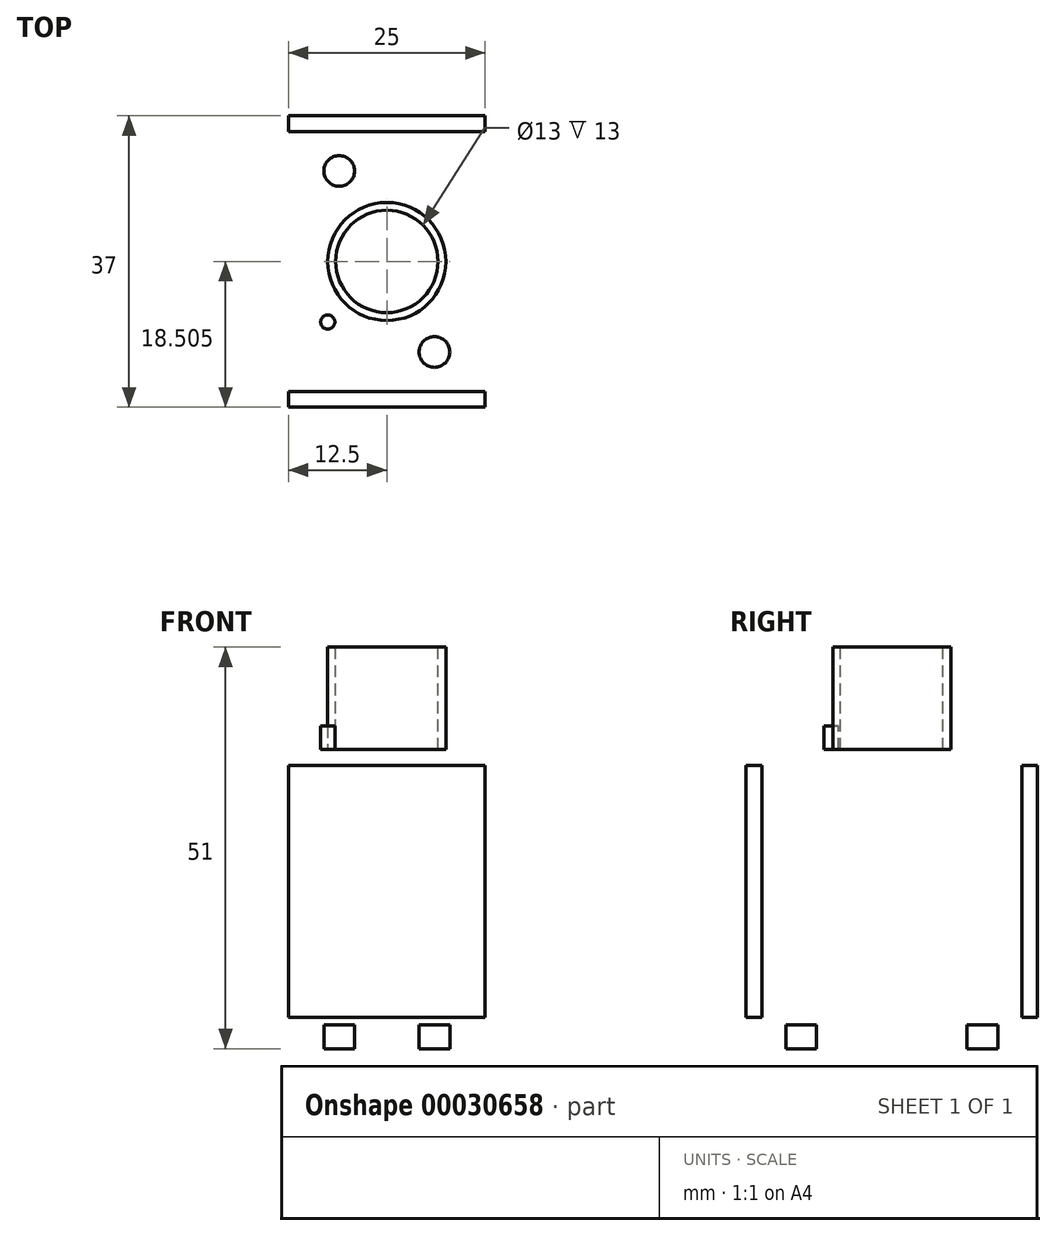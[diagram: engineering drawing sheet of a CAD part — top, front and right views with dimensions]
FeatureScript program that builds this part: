
annotation { "Feature Type Name" : "Feature", "Feature Type Description" : "" }
export const myFeature = defineFeature(function(context is Context, id is Id, definition is map)
    precondition{}
    {
        {
            var Q0;
            Q0=qCreatedBy(makeId("Right.planeOp"),FACE);
            var sketch = newSketch(context, id + "F0", { "sketchPlane" : qUnion([Q0])});
            skLineSegment(sketch, "E0.bottom", {"start": v(81.65, 0) * mm, "end": v(44.65, 0) * mm});
            skLineSegment(sketch, "E0.top", {"start": v(81.65, -41) * mm, "end": v(44.65, -41) * mm});
            skLineSegment(sketch, "E0.left", {"start": v(81.65, 0) * mm, "end": v(81.65, -41) * mm});
            skLineSegment(sketch, "E0.right", {"start": v(44.65, 0) * mm, "end": v(44.65, -41) * mm});
            skSolve(sketch);
        }
        {
            var Q0;
            Q0=makeQuery(id+"F0.imprint","IMPRINT",FACE,{"disambiguationData":[TD([[makeQuery(id+"F0.imprint","IMPRINT",EDGE,{"derivedFrom":sQuery(id+"F0.wireOp",EDGE,"E0.bottom")}),1.0]])]});
            extrude(context, id + "F1", {"entities" : qUnion([Q0]), "depth" : 25 * mm});
        }
        {
            var Q0;
            Q0=qCreatedBy(makeId("Right.planeOp"),FACE);
            var sketch = newSketch(context, id + "F2", { "sketchPlane" : qUnion([Q0])});
            skLineSegment(sketch, "E1.bottom", {"start": v(79.65, -38) * mm, "end": v(46.65, -38) * mm});
            skLineSegment(sketch, "E1.top", {"start": v(79.65, -3) * mm, "end": v(46.65, -3) * mm});
            skLineSegment(sketch, "E1.left", {"start": v(79.65, -38) * mm, "end": v(79.65, -3) * mm});
            skLineSegment(sketch, "E1.right", {"start": v(46.65, -38) * mm, "end": v(46.65, -3) * mm});
            skPoint(sketch, "E1.middle", {"position": v(63.15, -20.5) * mm});
            skPoint(sketch, "E1.middle.positionSnap0", {"position": v(81.63, -20.5) * mm});
            skPoint(sketch, "E1.centerSnap0", {"position": v(81.63, -20.5) * mm});
            skSolve(sketch);
        }
        {
            var Q0;
            Q0=makeQuery(id+"F2.imprint","IMPRINT",FACE,{"disambiguationData":[TD([[makeQuery(id+"F2.imprint","IMPRINT",EDGE,{"derivedFrom":sQuery(id+"F2.wireOp",EDGE,"u7z7irKr-tLwh-9OEY-cqf0-OPcKlIcIi4rX.bottom")}),1.0]])]});
            var Q1;
            Q1=makeQuery(id+"F2.imprint","IMPRINT",FACE,{"disambiguationData":[TD([[makeQuery(id+"F2.imprint","IMPRINT",EDGE,{"derivedFrom":sQuery(id+"F2.wireOp",EDGE,"E1.bottom")}),-1.0]])]});
            extrude(context, id + "F3", {"entities" : qUnion([Q0, Q1]), "operationType" : NewBodyOperationType.REMOVE, "depth" : 26 * mm});
        }
        {
            var Q0;
            Q0=qCreatedBy(makeId("Top.planeOp"),FACE);
            var sketch = newSketch(context, id + "F4", { "sketchPlane" : qUnion([Q0])});
            skLineSegment(sketch, "E2", {"start": v(0, 81.65) * mm, "end": v(0, 44.65) * mm});
            skLineSegment(sketch, "E3", {"start": v(0, 44.65) * mm, "end": v(25, 81.65) * mm});
            skCircle(sketch, "E4", {"center": v(12.5, 63.15) * mm, "radius": 7.5 * mm});
            skPoint(sketch, "E4.centerSnap0", {"position": v(0, 63.15) * mm});
            skCircle(sketch, "E5", {"center": v(12.5, 63.15) * mm, "radius": 6.5 * mm});
            skSolve(sketch);
        }
        {
            var Q0;
            {var subQ0=sQuery(id+"F4.wireOp",EDGE,"E5");var subQ1=sQuery(id+"F4.wireOp",EDGE,"E3");var subQ2=makeQuery(id+"F4.imprint","INTERSECT",VERTEX,{"disambiguationData":[OD(0.0)],"derivedFrom":[subQ1,subQ0]});Q0=makeQuery(id+"F4.imprint","IMPRINT",FACE,{"disambiguationData":[TD([[makeQuery(id+"F4.imprint","IMPRINT",EDGE,{"disambiguationData":[TD([[subQ2,-1.0]])],"derivedFrom":subQ1}),1.0]])]});}
            var Q1;
            {var subQ0=sQuery(id+"F4.wireOp",EDGE,"E5");var subQ1=sQuery(id+"F4.wireOp",EDGE,"E3");var subQ2=makeQuery(id+"F4.imprint","INTERSECT",VERTEX,{"disambiguationData":[OD(0.0)],"derivedFrom":[subQ1,subQ0]});Q1=makeQuery(id+"F4.imprint","IMPRINT",FACE,{"disambiguationData":[TD([[makeQuery(id+"F4.imprint","IMPRINT",EDGE,{"disambiguationData":[TD([[subQ2,-1.0]])],"derivedFrom":subQ1}),-1.0]])]});}
            extrude(context, id + "F5", {"entities" : qUnion([Q0, Q1]), "operationType" : NewBodyOperationType.REMOVE, "oppositeDirection" : true, "depth" : 25 * mm});
        }
        {
            var Q0;
            Q0 = qSketchRegion(id + "F4", true);
            extrude(context, id + "F6", {"entities" : qUnion([Q0]), "operationType" : NewBodyOperationType.ADD, "depth" : 10 * mm});
        }
        {
            var Q0;
            Q0=makeQuery(id+"F1.opExtrude","SWEPT_FACE",FACE,{"disambiguationData":[OSD([sQuery(id+"F0.wireOp",EDGE,"E0.top")])]});
            var sketch = newSketch(context, id + "F7", { "sketchPlane" : qUnion([Q0])});
            skCircle(sketch, "E6.MirrorC", {"center": v(18.55, -51.65) * mm, "radius": 1.95 * mm});
            skLineSegment(sketch, "E7", {"start": v(12.5, -44.65) * mm, "end": v(12.5, -81.65) * mm, "construction": true});
            skLineSegment(sketch, "E8", {"start": v(0, -63.15) * mm, "end": v(25, -63.15) * mm, "construction": true});
            skCircle(sketch, "E9.MirrorC", {"center": v(6.45, -51.65) * mm, "radius": 1.95 * mm});
            skCircle(sketch, "E10.MirrorC", {"center": v(18.55, -74.65) * mm, "radius": 1.95 * mm});
            skCircle(sketch, "E11.MirrorC", {"center": v(6.45, -74.65) * mm, "radius": 1.95 * mm});
            skSolve(sketch);
        }
        {
            var Q0;
            Q0=makeQuery(id+"F7.imprint","IMPRINT",FACE,{"disambiguationData":[TD([[makeQuery(id+"F7.imprint","IMPRINT",EDGE,{"derivedFrom":sQuery(id+"F7.wireOp",EDGE,"E9.MirrorC")}),1.0]])]});
            var Q1;
            Q1=makeQuery(id+"F7.imprint","IMPRINT",FACE,{"disambiguationData":[TD([[makeQuery(id+"F7.imprint","IMPRINT",EDGE,{"derivedFrom":sQuery(id+"F7.wireOp",EDGE,"E6.MirrorC")}),-1.0]])]});
            var Q2;
            Q2=makeQuery(id+"F7.imprint","IMPRINT",FACE,{"disambiguationData":[TD([[makeQuery(id+"F7.imprint","IMPRINT",EDGE,{"derivedFrom":sQuery(id+"F7.wireOp",EDGE,"E10.MirrorC")}),1.0]])]});
            var Q3;
            Q3=makeQuery(id+"F7.imprint","IMPRINT",FACE,{"disambiguationData":[TD([[makeQuery(id+"F7.imprint","IMPRINT",EDGE,{"derivedFrom":sQuery(id+"F7.wireOp",EDGE,"E11.MirrorC")}),-1.0]])]});
            extrude(context, id + "F8", {"entities" : qUnion([Q0, Q1, Q2, Q3]), "operationType" : NewBodyOperationType.REMOVE, "oppositeDirection" : true, "depth" : 4 * mm});
        }
        {
            var Q0;
            Q0=makeQuery(id+"F1.opExtrude","SWEPT_FACE",FACE,{"disambiguationData":[OSD([sQuery(id+"F0.wireOp",EDGE,"E0.bottom")])]});
            var sketch = newSketch(context, id + "F9", { "sketchPlane" : qUnion([Q0])});
            skCircle(sketch, "E12", {"center": v(20, 55.46) * mm, "radius": 0.9 * mm});
            skCircle(sketch, "E13.MirrorC", {"center": v(5, 55.46) * mm, "radius": 0.9 * mm});
            skPoint(sketch, "E14", {"position": v(12.5, 63.15) * mm});
            skSolve(sketch);
        }
        {
            var Q0;
            Q0=makeQuery(id+"F9.imprint","IMPRINT",FACE,{"disambiguationData":[TD([[makeQuery(id+"F9.imprint","IMPRINT",EDGE,{"derivedFrom":sQuery(id+"F9.wireOp",EDGE,"E13.MirrorC")}),-1.0]])]});
            var Q1;
            Q1=makeQuery(id+"F9.imprint","IMPRINT",FACE,{"disambiguationData":[TD([[makeQuery(id+"F9.imprint","IMPRINT",EDGE,{"derivedFrom":sQuery(id+"F9.wireOp",EDGE,"E12")}),1.0]])]});
            extrude(context, id + "F10", {"entities" : qUnion([Q0, Q1]), "operationType" : NewBodyOperationType.REMOVE, "oppositeDirection" : true, "depth" : 5 * mm});
        }
    });
